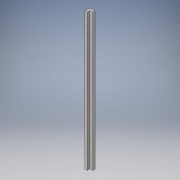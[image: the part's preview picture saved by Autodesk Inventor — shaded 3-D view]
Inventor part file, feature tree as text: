
AUTODESK INVENTOR PART (.ipt)
format: ipt  version: 2016 (Build 200138000, 138)  size: 92,672 bytes
history: native  units: in
note: dims shown in document units (in); Inventor stores cm internally (conversion verified against a paired STEP export)
features: extrude x1, sketch x1
ambient origin geometry x8: Origin, YZ Plane, XZ Plane, XY Plane, X Axis, Y Axis, Z Axis, Center Point
bodies: Solid1 (feature_tree)
feature tree (2):
  extrude  "Extrusion1"  Depth=53.75in TaperAngle=0.0deg
  sketch  "Sketch1"  dims[d2=2.0in d3=53.75in d4=0.0in]
